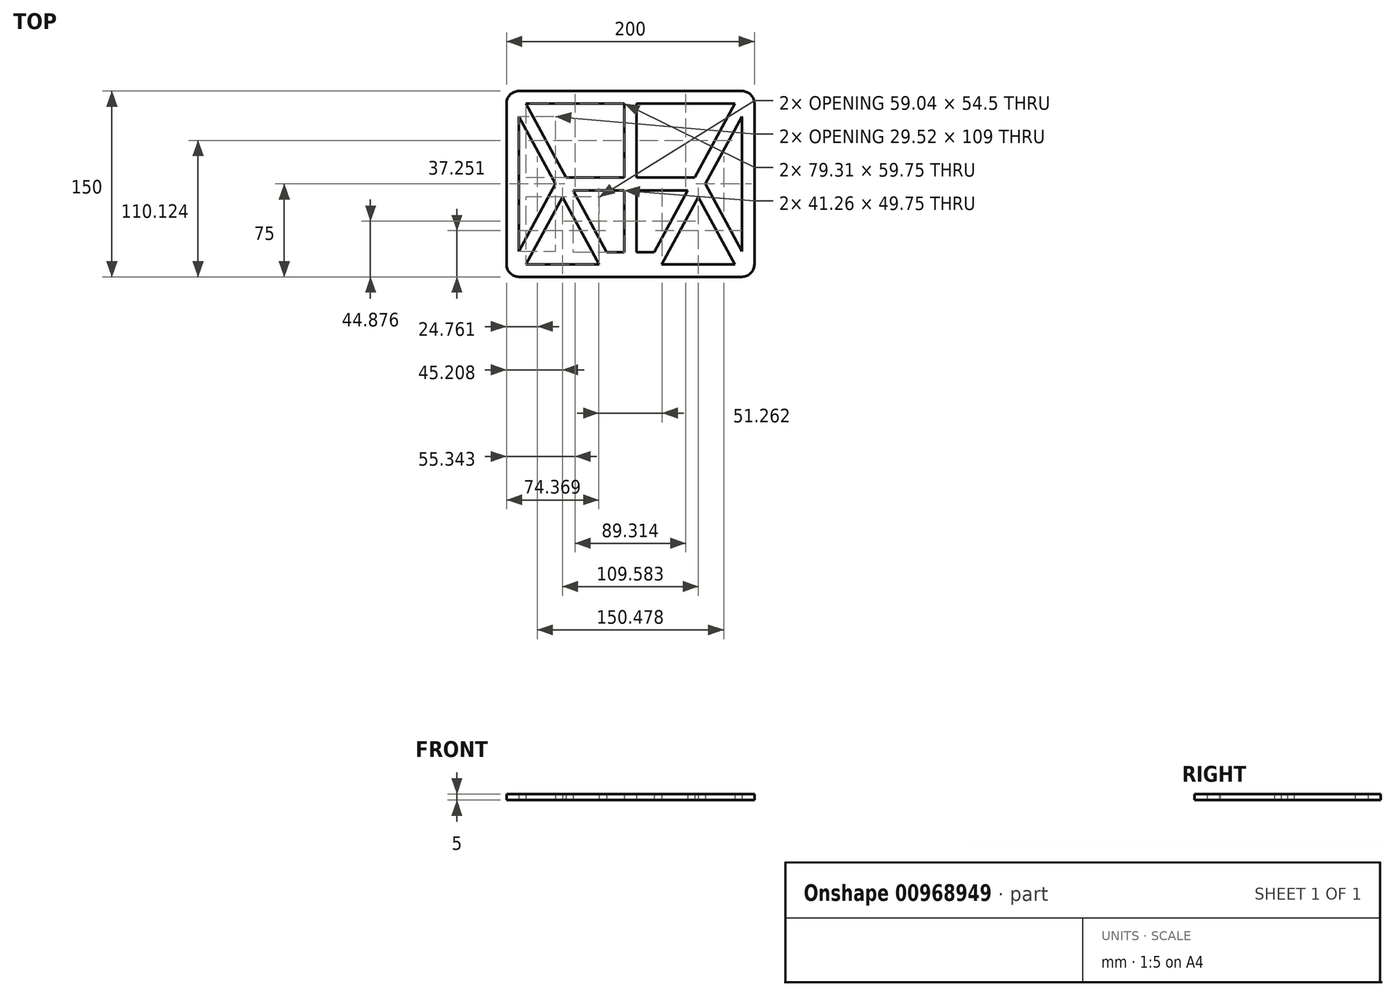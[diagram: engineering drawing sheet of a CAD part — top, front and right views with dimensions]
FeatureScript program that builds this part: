
annotation { "Feature Type Name" : "Feature", "Feature Type Description" : "" }
export const myFeature = defineFeature(function(context is Context, id is Id, definition is map)
    precondition{}
    {
        {
            var Q0;
            Q0=qCreatedBy(makeId("Top.planeOp"),FACE);
            var sketch = newSketch(context, id + "F0", { "sketchPlane" : qUnion([Q0])});
            skLineSegment(sketch, "E0.bottom", {"start": v(-100, 75) * mm, "end": v(100, 75) * mm});
            skLineSegment(sketch, "E0.top", {"start": v(-100, -75) * mm, "end": v(100, -75) * mm});
            skLineSegment(sketch, "E0.left", {"start": v(-100, 75) * mm, "end": v(-100, -75) * mm});
            skLineSegment(sketch, "E0.right", {"start": v(100, 75) * mm, "end": v(100, -75) * mm});
            skLineSegment(sketch, "E1.0", {"start": v(-90, 65) * mm, "end": v(90, 65) * mm});
            skLineSegment(sketch, "E1.1", {"start": v(-90, 65) * mm, "end": v(-90, -65) * mm});
            skLineSegment(sketch, "E1.2", {"start": v(-90, -65) * mm, "end": v(-25, -65) * mm});
            skLineSegment(sketch, "E1.3", {"start": v(90, 65) * mm, "end": v(90, -65) * mm});
            skLineSegment(sketch, "E2.top", {"start": v(-25, -55) * mm, "end": v(25, -55) * mm});
            skLineSegment(sketch, "E2.left", {"start": v(-25, -65) * mm, "end": v(-25, -55) * mm});
            skLineSegment(sketch, "E2.right", {"start": v(25, -65) * mm, "end": v(25, -55) * mm});
            skLineSegment(sketch, "E3.trimOffspring", {"start": v(25, -65) * mm, "end": v(90, -65) * mm});
            skLineSegment(sketch, "E4", {"start": v(-25, -55) * mm, "end": v(-90, 65) * mm, "construction": true});
            skLineSegment(sketch, "E5", {"start": v(25, -55) * mm, "end": v(90, 65) * mm, "construction": true});
            skLineSegment(sketch, "E6", {"start": v(0, -55) * mm, "end": v(0, 65) * mm, "construction": true});
            skLineSegment(sketch, "E7", {"start": v(-84.31, 65) * mm, "end": v(-19.31, -55) * mm});
            skLineSegment(sketch, "E8", {"start": v(-24.63, -66.17) * mm, "end": v(-90, 54.5) * mm});
            skLineSegment(sketch, "E9", {"start": v(-5, -55) * mm, "end": v(-5, 65) * mm});
            skLineSegment(sketch, "E10", {"start": v(5, 65) * mm, "end": v(5, -55) * mm});
            skLineSegment(sketch, "E11", {"start": v(24.13, -67.1) * mm, "end": v(90, 54.5) * mm});
            skLineSegment(sketch, "E12", {"start": v(19.31, -55) * mm, "end": v(84.31, 65) * mm});
            skLineSegment(sketch, "E13", {"start": v(-54.8, 0) * mm, "end": v(54.8, 0) * mm, "construction": true});
            skLineSegment(sketch, "E14", {"start": v(-54.8, 0) * mm, "end": v(-90, -65) * mm, "construction": true});
            skLineSegment(sketch, "E15", {"start": v(54.8, 0) * mm, "end": v(90, -65) * mm, "construction": true});
            skLineSegment(sketch, "E16", {"start": v(0, 5.25) * mm, "end": v(57.63, 5.25) * mm});
            skLineSegment(sketch, "E17", {"start": v(57.63, 5.25) * mm, "end": v(90, -54.5) * mm});
            skLineSegment(sketch, "E18", {"start": v(0, -5.25) * mm, "end": v(51.95, -5.25) * mm});
            skLineSegment(sketch, "E19", {"start": v(51.95, -5.25) * mm, "end": v(84.31, -65) * mm});
            skLineSegment(sketch, "E20", {"start": v(0, -5.25) * mm, "end": v(-51.95, -5.25) * mm});
            skLineSegment(sketch, "E21", {"start": v(-51.95, -5.25) * mm, "end": v(-84.31, -65) * mm});
            skLineSegment(sketch, "E22", {"start": v(0, 5.25) * mm, "end": v(-57.63, 5.25) * mm});
            skLineSegment(sketch, "E23", {"start": v(-57.63, 5.25) * mm, "end": v(-90, -54.5) * mm});
            skSolve(sketch);
        }
        {
            var Q0;
            Q0=makeQuery(id+"F0.imprint","IMPRINT",FACE,{"disambiguationData":[TD([[makeQuery(id+"F0.imprint","IMPRINT",EDGE,{"derivedFrom":sQuery(id+"F0.wireOp",EDGE,"E0.bottom")}),-1.0]])]});
            var Q1;
            {var subQ0=sQuery(id+"F0.wireOp",EDGE,"E2.left");Q1=makeQuery(id+"F0.imprint","IMPRINT",FACE,{"disambiguationData":[TD([[makeQuery(id+"F0.imprint","IMPRINT",EDGE,{"derivedFrom":subQ0}),1.0]])]});}
            var Q2;
            {var subQ0=sQuery(id+"F0.wireOp",EDGE,"E9");Q2=makeQuery(id+"F0.imprint","IMPRINT",FACE,{"disambiguationData":[TD([[makeQuery(id+"F0.imprint","IMPRINT",EDGE,{"derivedFrom":subQ0}),-1.0]])]});}
            var Q3;
            {var subQ0=sQuery(id+"F0.wireOp",EDGE,"E2.right");Q3=makeQuery(id+"F0.imprint","IMPRINT",FACE,{"disambiguationData":[TD([[makeQuery(id+"F0.imprint","IMPRINT",EDGE,{"derivedFrom":subQ0}),-1.0]])]});}
            var Q4;
            {var subQ1=sQuery(id+"F0.wireOp",EDGE,"E1.2");var subQ7=sQuery(id+"F0.wireOp",EDGE,"E1.1");var subQ9=makeQuery(id+"F0.imprint","INTERSECT",VERTEX,{"derivedFrom":[subQ7,subQ1]});Q4=makeQuery(id+"F0.imprint","IMPRINT",FACE,{"disambiguationData":[TD([[makeQuery(id+"F0.imprint","IMPRINT",EDGE,{"disambiguationData":[TD([[subQ9,1.0]])],"derivedFrom":subQ7}),1.0]])]});}
            var Q5;
            {var subQ1=sQuery(id+"F0.wireOp",EDGE,"E1.1");var subQ6=sQuery(id+"F0.wireOp",EDGE,"E1.0");var subQ10=makeQuery(id+"F0.imprint","INTERSECT",VERTEX,{"derivedFrom":[subQ6,subQ1]});Q5=makeQuery(id+"F0.imprint","IMPRINT",FACE,{"disambiguationData":[TD([[makeQuery(id+"F0.imprint","IMPRINT",EDGE,{"disambiguationData":[TD([[subQ10,-1.0]])],"derivedFrom":subQ6}),-1.0]])]});}
            var Q6;
            {var subQ3=sQuery(id+"F0.wireOp",EDGE,"E7");var subQ9=sQuery(id+"F0.wireOp",EDGE,"E22");var subQ10=makeQuery(id+"F0.imprint","INTERSECT",VERTEX,{"derivedFrom":[subQ3,subQ9]});Q6=makeQuery(id+"F0.imprint","IMPRINT",FACE,{"disambiguationData":[TD([[makeQuery(id+"F0.imprint","IMPRINT",EDGE,{"disambiguationData":[TD([[subQ10,-1.0]])],"derivedFrom":subQ3}),-1.0]])]});}
            var Q7;
            {var subQ0=sQuery(id+"F0.wireOp",EDGE,"E20");var subQ9=sQuery(id+"F0.wireOp",EDGE,"E9");var subQ10=makeQuery(id+"F0.imprint","INTERSECT",VERTEX,{"derivedFrom":[subQ9,subQ0]});Q7=makeQuery(id+"F0.imprint","IMPRINT",FACE,{"disambiguationData":[TD([[makeQuery(id+"F0.imprint","IMPRINT",EDGE,{"disambiguationData":[TD([[subQ10,-1.0]])],"derivedFrom":subQ9}),-1.0]])]});}
            var Q8;
            {var subQ0=sQuery(id+"F0.wireOp",EDGE,"E22");var subQ1=sQuery(id+"F0.wireOp",EDGE,"E7");var subQ2=makeQuery(id+"F0.imprint","INTERSECT",VERTEX,{"derivedFrom":[subQ1,subQ0]});Q8=makeQuery(id+"F0.imprint","IMPRINT",FACE,{"disambiguationData":[TD([[makeQuery(id+"F0.imprint","IMPRINT",EDGE,{"disambiguationData":[TD([[subQ2,-1.0]])],"derivedFrom":subQ1}),1.0]])]});}
            var Q9;
            {var subQ0=sQuery(id+"F0.wireOp",EDGE,"E16");var subQ1=sQuery(id+"F0.wireOp",EDGE,"E10");var subQ2=makeQuery(id+"F0.imprint","INTERSECT",VERTEX,{"derivedFrom":[subQ1,subQ0]});Q9=makeQuery(id+"F0.imprint","IMPRINT",FACE,{"disambiguationData":[TD([[makeQuery(id+"F0.imprint","IMPRINT",EDGE,{"disambiguationData":[TD([[subQ2,-1.0]])],"derivedFrom":subQ1}),1.0]])]});}
            var Q10;
            {var subQ5=sQuery(id+"F0.wireOp",EDGE,"E11");var subQ9=sQuery(id+"F0.wireOp",EDGE,"E19");var subQ10=makeQuery(id+"F0.imprint","INTERSECT",VERTEX,{"derivedFrom":[subQ5,subQ9]});Q10=makeQuery(id+"F0.imprint","IMPRINT",FACE,{"disambiguationData":[TD([[makeQuery(id+"F0.imprint","IMPRINT",EDGE,{"disambiguationData":[TD([[subQ10,-1.0]])],"derivedFrom":subQ5}),1.0]])]});}
            var Q11;
            {var subQ1=sQuery(id+"F0.wireOp",EDGE,"E1.3");var subQ5=sQuery(id+"F0.wireOp",EDGE,"E3.trimOffspring");var subQ6=makeQuery(id+"F0.imprint","INTERSECT",VERTEX,{"derivedFrom":[subQ1,subQ5]});Q11=makeQuery(id+"F0.imprint","IMPRINT",FACE,{"disambiguationData":[TD([[makeQuery(id+"F0.imprint","IMPRINT",EDGE,{"disambiguationData":[TD([[subQ6,1.0]])],"derivedFrom":subQ1}),-1.0]])]});}
            var Q12;
            {var subQ1=sQuery(id+"F0.wireOp",EDGE,"E1.3");var subQ6=sQuery(id+"F0.wireOp",EDGE,"E1.0");var subQ10=makeQuery(id+"F0.imprint","INTERSECT",VERTEX,{"derivedFrom":[subQ6,subQ1]});Q12=makeQuery(id+"F0.imprint","IMPRINT",FACE,{"disambiguationData":[TD([[makeQuery(id+"F0.imprint","IMPRINT",EDGE,{"disambiguationData":[TD([[subQ10,1.0]])],"derivedFrom":subQ6}),-1.0]])]});}
            extrude(context, id + "F1", {"entities" : qUnion([Q0, Q1, Q2, Q3, Q4, Q5, Q6, Q7, Q8, Q9, Q10, Q11, Q12]), "depth" : 5 * mm, "offsetDistance" : 25 * mm});
        }
        {
            var Q0;
            Q0=makeQuery(id+"F1.opExtrude","SWEPT_EDGE",EDGE,{"disambiguationData":[OSD([sQuery(id+"F0.wireOp",EDGE,"E0.top"),sQuery(id+"F0.wireOp",EDGE,"E0.left")])]});
            var Q1;
            Q1=makeQuery(id+"F1.opExtrude","SWEPT_EDGE",EDGE,{"disambiguationData":[OSD([sQuery(id+"F0.wireOp",EDGE,"E0.top"),sQuery(id+"F0.wireOp",EDGE,"E0.right")])]});
            var Q2;
            Q2=makeQuery(id+"F1.opExtrude","SWEPT_EDGE",EDGE,{"disambiguationData":[OSD([sQuery(id+"F0.wireOp",EDGE,"E0.bottom"),sQuery(id+"F0.wireOp",EDGE,"E0.right")])]});
            var Q3;
            Q3=makeQuery(id+"F1.opExtrude","SWEPT_EDGE",EDGE,{"disambiguationData":[OSD([sQuery(id+"F0.wireOp",EDGE,"E0.bottom"),sQuery(id+"F0.wireOp",EDGE,"E0.left")])]});
            fillet(context, id + "F2", {"entities" : qUnion([Q0, Q1, Q2, Q3]), "radius" : 10 * mm, "tangentPropagation" : true, "allowEdgeOverflow" : false});
        }
    });
